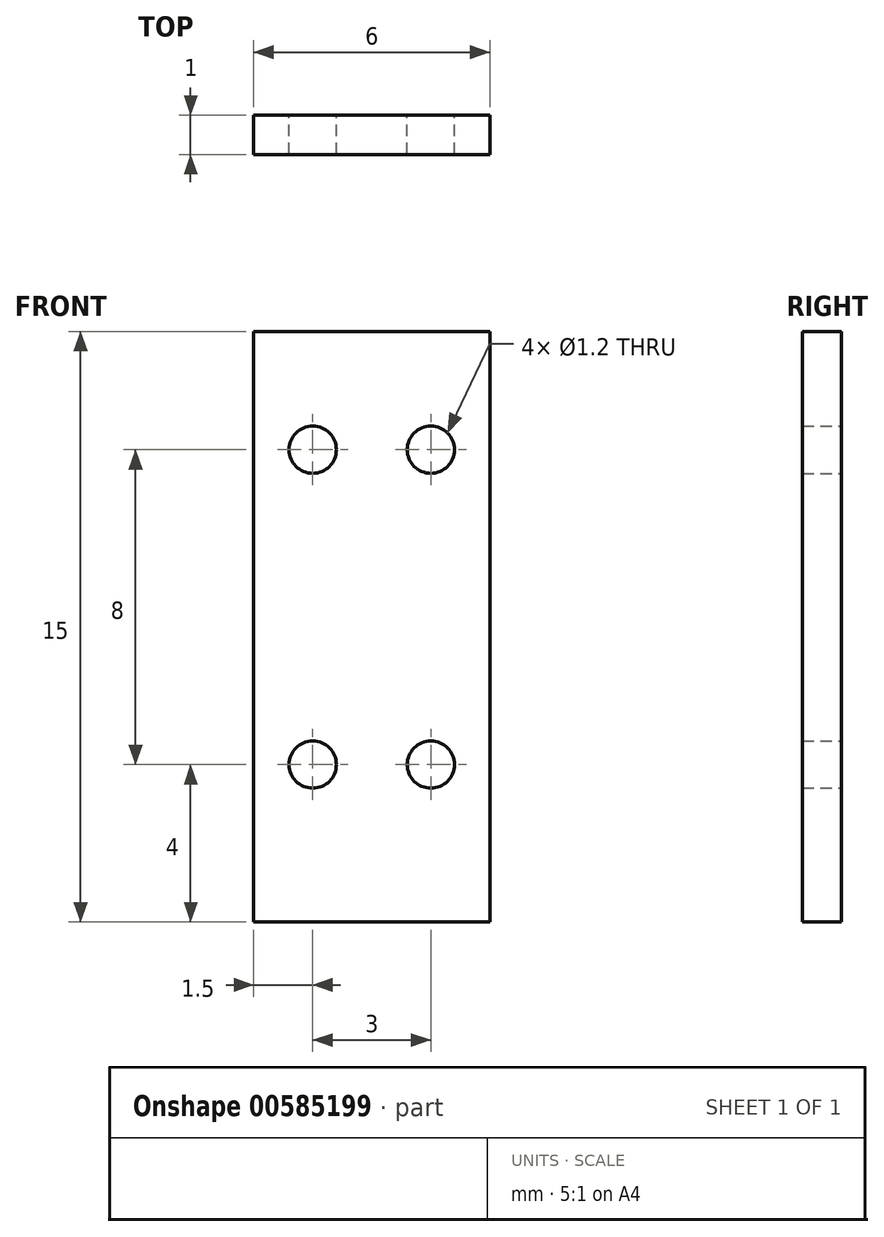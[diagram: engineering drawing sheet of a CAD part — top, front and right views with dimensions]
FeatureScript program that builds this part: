
annotation { "Feature Type Name" : "Feature", "Feature Type Description" : "" }
export const myFeature = defineFeature(function(context is Context, id is Id, definition is map)
    precondition{}
    {
        {
            var Q0;
            Q0=qCreatedBy(makeId("Front.planeOp"),FACE);
            var sketch = newSketch(context, id + "F0", { "sketchPlane" : qUnion([Q0])});
            skLineSegment(sketch, "E0", {"start": v(-5.74, 12) * mm, "end": v(6.48, 12) * mm, "construction": true});
            skLineSegment(sketch, "E1", {"start": v(-5.74, 4) * mm, "end": v(6.38, 4) * mm, "construction": true});
            skLineSegment(sketch, "E2", {"start": v(0, 0) * mm, "end": v(0, 18.14) * mm, "construction": true});
            skLineSegment(sketch, "E3.bottom", {"start": v(-3, 15) * mm, "end": v(3, 15) * mm});
            skLineSegment(sketch, "E3.top", {"start": v(-3, 0) * mm, "end": v(3, 0) * mm});
            skLineSegment(sketch, "E3.left", {"start": v(-3, 15) * mm, "end": v(-3, 0) * mm});
            skLineSegment(sketch, "E3.right", {"start": v(3, 15) * mm, "end": v(3, 0) * mm});
            skLineSegment(sketch, "E4", {"start": v(1.5, 0) * mm, "end": v(1.5, 16.93) * mm, "construction": true});
            skLineSegment(sketch, "E5", {"start": v(-1.5, 0) * mm, "end": v(-1.5, 16.93) * mm, "construction": true});
            skCircle(sketch, "E6", {"center": v(1.5, 12) * mm, "radius": 0.6 * mm});
            skCircle(sketch, "E7", {"center": v(-1.5, 12) * mm, "radius": 0.6 * mm});
            skCircle(sketch, "E8", {"center": v(-1.5, 4) * mm, "radius": 0.6 * mm});
            skCircle(sketch, "E9", {"center": v(1.5, 4) * mm, "radius": 0.6 * mm});
            skSolve(sketch);
        }
        {
            var Q0;
            Q0 = qSketchRegion(id + "F0", true);
            extrude(context, id + "F1", {"entities" : qUnion([Q0]), "depth" : 1 * mm, "offsetDistance" : 25 * mm});
        }
    });
